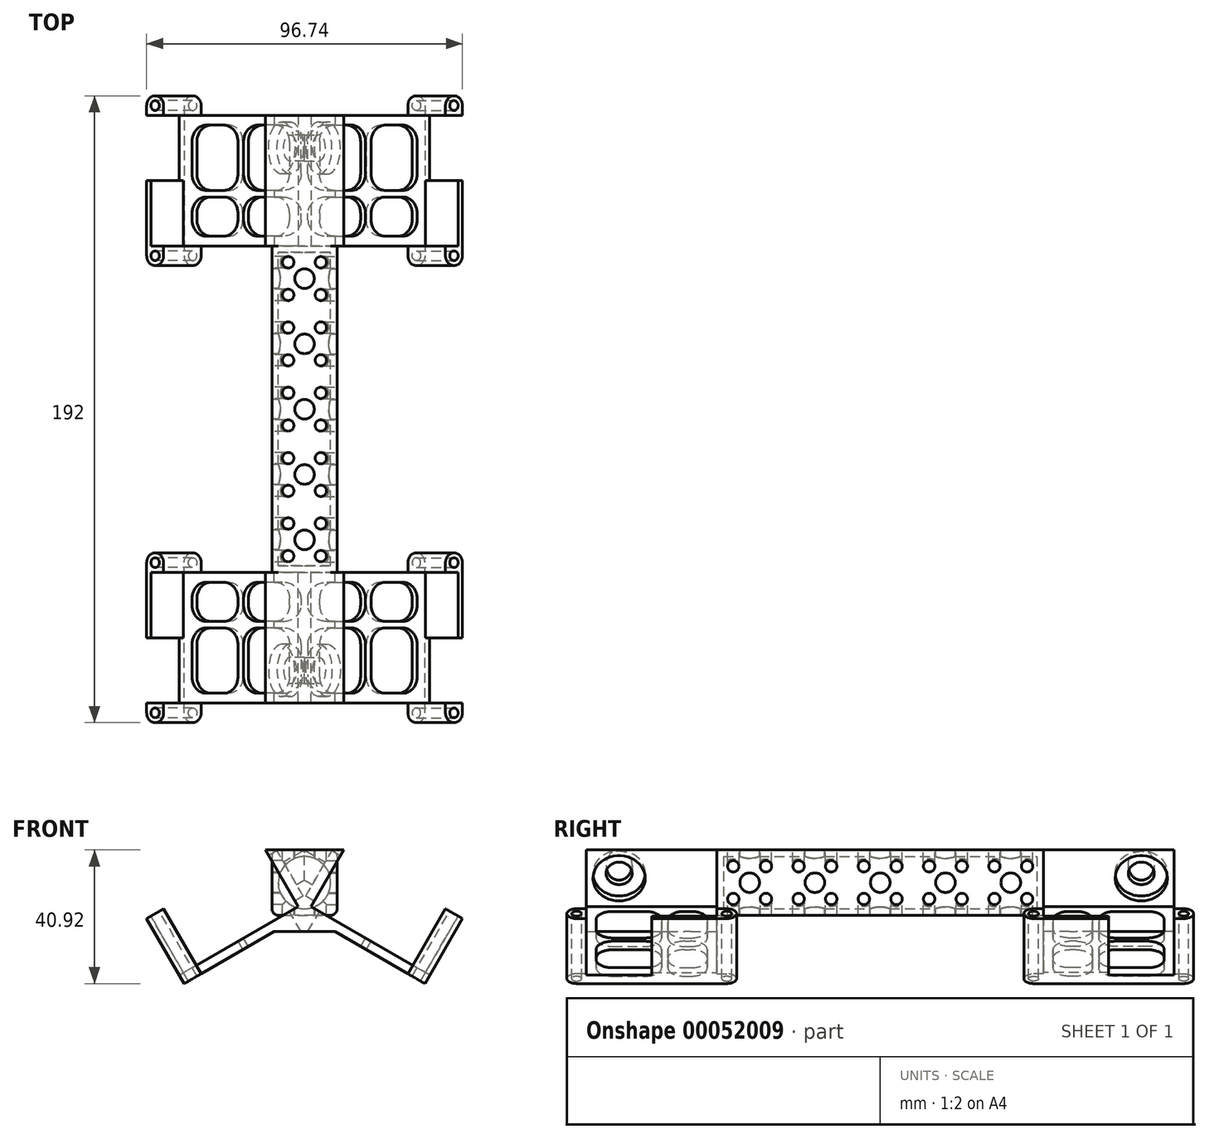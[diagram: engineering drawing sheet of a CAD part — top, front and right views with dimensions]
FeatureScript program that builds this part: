
annotation { "Feature Type Name" : "Feature", "Feature Type Description" : "" }
export const myFeature = defineFeature(function(context is Context, id is Id, definition is map)
    precondition{}
    {
        {
            var Q0;
            Q0=qCreatedBy(makeId("Front.planeOp"),FACE);
            var sketch = newSketch(context, id + "F0", { "sketchPlane" : qUnion([Q0])});
            skLineSegment(sketch, "E0.bottom", {"start": v(0, 10) * mm, "end": v(10, 10) * mm});
            skLineSegment(sketch, "E0.top", {"start": v(0, -10) * mm, "end": v(10, -10) * mm});
            skLineSegment(sketch, "E0.left", {"start": v(0, 10) * mm, "end": v(0, -10) * mm});
            skLineSegment(sketch, "E0.right", {"start": v(10, 10) * mm, "end": v(10, -10) * mm});
            skPoint(sketch, "E1", {"position": v(0, 0) * mm});
            skSolve(sketch);
        }
        {
            var Q0;
            Q0=makeQuery(id+"F0.imprint","IMPRINT",FACE,{"disambiguationData":[TD([[makeQuery(id+"F0.imprint","IMPRINT",EDGE,{"derivedFrom":sQuery(id+"F0.wireOp",EDGE,"E0.bottom")}),-1.0]])]});
            extrude(context, id + "F1", {"entities" : qUnion([Q0]), "depth" : 50 * mm, "offsetDistance" : 25 * mm});
        }
        {
            var Q0;
            Q0=makeQuery(id+"F1.opExtrude","CAP_FACE",FACE,{"disambiguationData":[OSD([sQuery(id+"F0.wireOp",EDGE,"E0.bottom"),sQuery(id+"F0.wireOp",EDGE,"E0.top"),sQuery(id+"F0.wireOp",EDGE,"E0.left"),sQuery(id+"F0.wireOp",EDGE,"E0.right")])],"isStart":false});
            var sketch = newSketch(context, id + "F2", { "sketchPlane" : qUnion([Q0])});
            skLineSegment(sketch, "E2", {"start": v(12, 10) * mm, "end": v(0.5, -9.92) * mm});
            skLineSegment(sketch, "E3", {"start": v(0.5, -9.92) * mm, "end": v(36.87, -30.92) * mm});
            skLineSegment(sketch, "E4", {"start": v(36.87, -30.92) * mm, "end": v(48.37, -11) * mm});
            skLineSegment(sketch, "E5", {"start": v(48.37, -11) * mm, "end": v(12, 10) * mm});
            skLineSegment(sketch, "E6", {"start": v(12, 10) * mm, "end": v(10, 10) * mm});
            skLineSegment(sketch, "E7", {"start": v(9.3, -15) * mm, "end": v(0, -15) * mm});
            skLineSegment(sketch, "E8", {"start": v(0, -15) * mm, "end": v(0, -10) * mm});
            skSolve(sketch);
        }
        {
            var Q0;
            {var subQ4=makeQuery(id+"F1.opExtrude","CAP_EDGE",EDGE,{"disambiguationData":[OSD([sQuery(id+"F0.wireOp",EDGE,"E0.bottom")])],"isStart":false});Q0=makeQuery(id+"F2.imprint","IMPRINT",FACE,{"disambiguationData":[TD([[makeQuery(id+"F2.imprint","IMPRINT",EDGE,{"derivedFrom":subQ4}),-1.0]])]});}
            var Q1;
            Q1=makeQuery(id+"F2.imprint","IMPRINT",FACE,{"disambiguationData":[TD([[makeQuery(id+"F2.imprint","IMPRINT",EDGE,{"derivedFrom":sQuery(id+"F2.wireOp",EDGE,"E3")}),1.0]])]});
            var Q2;
            {var subQ1=makeQuery(id+"F1.opExtrude","CAP_EDGE",EDGE,{"disambiguationData":[OSD([sQuery(id+"F0.wireOp",EDGE,"E0.top")])],"isStart":false});Q2=makeQuery(id+"F2.imprint","IMPRINT",FACE,{"disambiguationData":[TD([[makeQuery(id+"F2.imprint","IMPRINT",EDGE,{"derivedFrom":subQ1}),1.0]])]});}
            var Q3;
            {var subQ0=sQuery(id+"F2.wireOp",EDGE,"E6");Q3=makeQuery(id+"F2.imprint","IMPRINT",FACE,{"disambiguationData":[TD([[makeQuery(id+"F2.imprint","IMPRINT",EDGE,{"derivedFrom":subQ0}),1.0]])]});}
            var Q4;
            {var subQ0=sQuery(id+"F2.wireOp",EDGE,"E4");Q4=makeQuery(id+"F2.imprint","IMPRINT",FACE,{"disambiguationData":[TD([[makeQuery(id+"F2.imprint","IMPRINT",EDGE,{"derivedFrom":subQ0}),1.0]])]});}
            var Q5;
            {var subQ0=sQuery(id+"F2.wireOp",EDGE,"E7");Q5=makeQuery(id+"F2.imprint","IMPRINT",FACE,{"disambiguationData":[TD([[makeQuery(id+"F2.imprint","IMPRINT",EDGE,{"derivedFrom":subQ0}),-1.0]])]});}
            extrude(context, id + "F3", {"entities" : qUnion([Q0, Q1, Q2, Q3, Q4, Q5]), "operationType" : NewBodyOperationType.ADD, "depth" : 40 * mm, "offsetDistance" : 25 * mm});
        }
        {
            var Q0;
            Q0=makeQuery(id+"F3.opExtrude","SWEPT_FACE",FACE,{"disambiguationData":[OSD([sQuery(id+"F2.wireOp",EDGE,"E5")])]});
            var sketch = newSketch(context, id + "F4", { "sketchPlane" : qUnion([Q0])});
            skLineSegment(sketch, "E9.bottom", {"start": v(5.4, -90) * mm, "end": v(45.9, -90) * mm});
            skLineSegment(sketch, "E9.top", {"start": v(5.4, -50) * mm, "end": v(45.9, -50) * mm});
            skLineSegment(sketch, "E9.left", {"start": v(5.4, -90) * mm, "end": v(5.4, -50) * mm});
            skLineSegment(sketch, "E9.right", {"start": v(45.9, -90) * mm, "end": v(45.9, -50) * mm});
            skPoint(sketch, "E10", {"position": v(5.4, -70) * mm});
            skLineSegment(sketch, "E11.bottom", {"start": v(47.4, -90) * mm, "end": v(45.9, -90) * mm});
            skLineSegment(sketch, "E11.top", {"start": v(47.4, -70) * mm, "end": v(45.9, -70) * mm});
            skLineSegment(sketch, "E11.left", {"start": v(47.4, -90) * mm, "end": v(47.4, -70) * mm});
            skLineSegment(sketch, "E11.right", {"start": v(45.9, -90) * mm, "end": v(45.9, -70) * mm});
            skCircle(sketch, "E12", {"center": v(44.4, -93) * mm, "radius": 1.5 * mm});
            skCircle(sketch, "E13", {"center": v(44.4, -93) * mm, "radius": 3 * mm});
            skCircle(sketch, "E14", {"center": v(44.4, -47) * mm, "radius": 1.5 * mm});
            skCircle(sketch, "E15", {"center": v(44.4, -47) * mm, "radius": 3 * mm});
            skLineSegment(sketch, "E16", {"start": v(47.4, -90) * mm, "end": v(47.4, -93) * mm});
            skLineSegment(sketch, "E17", {"start": v(47.4, -50) * mm, "end": v(47.4, -47) * mm});
            skLineSegment(sketch, "E18", {"start": v(41.4, -93) * mm, "end": v(41.4, -90) * mm});
            skLineSegment(sketch, "E19", {"start": v(41.4, -47) * mm, "end": v(41.4, -50) * mm});
            skSolve(sketch);
        }
        {
            var Q0;
            Q0=makeQuery(id+"F4.imprint","IMPRINT",FACE,{"disambiguationData":[TD([[makeQuery(id+"F4.imprint","IMPRINT",EDGE,{"derivedFrom":sQuery(id+"F4.wireOp",EDGE,"E12")}),-1.0]])]});
            var Q1;
            Q1=makeQuery(id+"F4.imprint","IMPRINT",FACE,{"disambiguationData":[TD([[makeQuery(id+"F4.imprint","IMPRINT",EDGE,{"derivedFrom":sQuery(id+"F4.wireOp",EDGE,"E14")}),-1.0]])]});
            var Q2;
            {var subQ0=sQuery(id+"F4.wireOp",EDGE,"E19");Q2=makeQuery(id+"F4.imprint","IMPRINT",FACE,{"disambiguationData":[TD([[makeQuery(id+"F4.imprint","IMPRINT",EDGE,{"derivedFrom":subQ0}),1.0]])]});}
            var Q3;
            {var subQ6=sQuery(id+"F4.wireOp",EDGE,"E17");Q3=makeQuery(id+"F4.imprint","IMPRINT",FACE,{"disambiguationData":[TD([[makeQuery(id+"F4.imprint","IMPRINT",EDGE,{"derivedFrom":subQ6}),1.0]])]});}
            var Q4;
            {var subQ0=sQuery(id+"F4.wireOp",EDGE,"E18");Q4=makeQuery(id+"F4.imprint","IMPRINT",FACE,{"disambiguationData":[TD([[makeQuery(id+"F4.imprint","IMPRINT",EDGE,{"derivedFrom":subQ0}),-1.0]])]});}
            var Q5;
            {var subQ0=sQuery(id+"F4.wireOp",EDGE,"E11.bottom");Q5=makeQuery(id+"F4.imprint","IMPRINT",FACE,{"disambiguationData":[TD([[makeQuery(id+"F4.imprint","IMPRINT",EDGE,{"derivedFrom":subQ0}),1.0]])]});}
            var Q6;
            Q6=makeQuery(id+"F3.opExtrude","SWEPT_FACE",FACE,{"disambiguationData":[OSD([sQuery(id+"F2.wireOp",EDGE,"E3")])]});
            extrude(context, id + "F5", {"entities" : qUnion([Q0, Q1, Q2, Q3, Q4, Q5]), "operationType" : NewBodyOperationType.ADD, "endBound" : BoundingType.UP_TO_SURFACE, "oppositeDirection" : true, "depth" : 25 * mm, "endBoundEntityFace" : qUnion([Q6]), "offsetDistance" : 25 * mm});
        }
        {
            var Q0;
            {var subQ0=sQuery(id+"F2.wireOp",EDGE,"E5");Q0=makeQuery(id+"F5.boolean.opBoolean","MERGE",FACE,{"derivedFrom":[makeQuery(id+"F3.opExtrude","SWEPT_FACE",FACE,{"disambiguationData":[OSD([subQ0])]}),makeQuery(id+"F5.opExtrude","CAP_FACE",FACE,{"disambiguationData":[OSD([sQuery(id+"F4.wireOp",EDGE,"E9.bottom"),sQuery(id+"F4.wireOp",EDGE,"E11.bottom"),sQuery(id+"F4.wireOp",EDGE,"E12"),sQuery(id+"F4.wireOp",EDGE,"E13"),sQuery(id+"F4.wireOp",EDGE,"E16"),sQuery(id+"F4.wireOp",EDGE,"E18")])],"isStart":true}),makeQuery(id+"F5.opExtrude","CAP_FACE",FACE,{"disambiguationData":[OSD([subQ0,sQuery(id+"F4.wireOp",EDGE,"E9.top"),sQuery(id+"F4.wireOp",EDGE,"E14"),sQuery(id+"F4.wireOp",EDGE,"E15"),sQuery(id+"F4.wireOp",EDGE,"E17"),sQuery(id+"F4.wireOp",EDGE,"E19")])],"isStart":true})]});}
            var sketch = newSketch(context, id + "F6", { "sketchPlane" : qUnion([Q0])});
            skLineSegment(sketch, "E20.bottom", {"start": v(5.4, -90) * mm, "end": v(45.9, -90) * mm});
            skLineSegment(sketch, "E20.top", {"start": v(5.4, -50) * mm, "end": v(45.9, -50) * mm});
            skLineSegment(sketch, "E20.left", {"start": v(5.4, -90) * mm, "end": v(5.4, -50) * mm});
            skLineSegment(sketch, "E20.right", {"start": v(45.9, -90) * mm, "end": v(45.9, -50) * mm});
            skPoint(sketch, "E21", {"position": v(5.4, -70) * mm});
            skLineSegment(sketch, "E22.bottom", {"start": v(47.4, -90) * mm, "end": v(45.9, -90) * mm});
            skLineSegment(sketch, "E22.top", {"start": v(47.4, -70) * mm, "end": v(45.9, -70) * mm});
            skLineSegment(sketch, "E22.left", {"start": v(47.4, -90) * mm, "end": v(47.4, -70) * mm});
            skLineSegment(sketch, "E22.right", {"start": v(45.9, -90) * mm, "end": v(45.9, -70) * mm});
            skCircle(sketch, "E23", {"center": v(44.4, -93) * mm, "radius": 1.5 * mm});
            skCircle(sketch, "E24", {"center": v(44.4, -93) * mm, "radius": 3 * mm});
            skCircle(sketch, "E25", {"center": v(44.4, -47) * mm, "radius": 1.5 * mm});
            skCircle(sketch, "E26", {"center": v(44.4, -47) * mm, "radius": 3 * mm});
            skLineSegment(sketch, "E27", {"start": v(47.4, -90) * mm, "end": v(47.4, -93) * mm});
            skLineSegment(sketch, "E28", {"start": v(47.4, -60) * mm, "end": v(47.4, -47) * mm});
            skLineSegment(sketch, "E29", {"start": v(41.4, -93) * mm, "end": v(41.4, -90) * mm});
            skLineSegment(sketch, "E30", {"start": v(41.4, -47) * mm, "end": v(41.4, -50) * mm});
            skSolve(sketch);
        }
        {
            var Q0;
            Q0=makeQuery(id+"F6.imprint","IMPRINT",FACE,{"disambiguationData":[TD([[makeQuery(id+"F6.imprint","IMPRINT",EDGE,{"derivedFrom":sQuery(id+"F6.wireOp",EDGE,"E22.bottom")}),-1.0]])]});
            var Q1;
            {var subQ0=sQuery(id+"F6.wireOp",EDGE,"E20.left");Q1=makeQuery(id+"F6.imprint","IMPRINT",FACE,{"disambiguationData":[TD([[makeQuery(id+"F6.imprint","IMPRINT",EDGE,{"derivedFrom":subQ0}),-1.0]])]});}
            extrude(context, id + "F7", {"entities" : qUnion([Q0, Q1]), "operationType" : NewBodyOperationType.REMOVE, "oppositeDirection" : true, "depth" : 20 * mm, "offsetDistance" : 25 * mm});
        }
        {
            var Q0;
            Q0=makeQuery(id+"F7.boolean.opBoolean","COPY",FACE,{"derivedFrom":makeQuery(id+"F7.opExtrude","SWEPT_FACE",FACE,{"disambiguationData":[OSD([sQuery(id+"F6.wireOp",EDGE,"E20.left")])]})});
            var sketch = newSketch(context, id + "F8", { "sketchPlane" : qUnion([Q0])});
            skLineSegment(sketch, "E31.bottom", {"start": v(-90, 14.66) * mm, "end": v(-70, 14.66) * mm});
            skLineSegment(sketch, "E31.top", {"start": v(-90, -5.34) * mm, "end": v(-70, -5.34) * mm});
            skLineSegment(sketch, "E31.left", {"start": v(-90, 14.66) * mm, "end": v(-90, -5.34) * mm});
            skLineSegment(sketch, "E31.right", {"start": v(-70, 14.66) * mm, "end": v(-70, -5.34) * mm});
            skLineSegment(sketch, "E32", {"start": v(-90, 14.66) * mm, "end": v(-70, -5.34) * mm});
            skPoint(sketch, "E33", {"position": v(-80, 4.66) * mm});
            skSolve(sketch);
        }
        {
            var Q0;
            Q0=sQuery(id+"F8.wireOp",VERTEX,"E33");
            var Q1;
            Q1=makeQuery(id+"F1.opExtrude","SWEPT_BODY",BODY,{"disambiguationData":[OSD([sQuery(id+"F0.wireOp",EDGE,"E0.bottom"),sQuery(id+"F0.wireOp",EDGE,"E0.top"),sQuery(id+"F0.wireOp",EDGE,"E0.left"),sQuery(id+"F0.wireOp",EDGE,"E0.right")])]});
            hole(context, id + "F9", {"style" : HoleStyle.C_BORE, "endStyle" : HoleEndStyle.BLIND, "holeDiameter" : 8 * mm, "cBoreDiameter" : 16 * mm, "cBoreDepth" : 3 * mm, "majorDiameter" : 5 * mm, "holeDepth" : 10 * mm, "isTappedThrough" : true, "tappedDepth" : 12 * mm, "tapClearance" : 3, "locations" : qUnion([Q0]), "scope" : qUnion([Q1])});
        }
        {
            var Q0;
            Q0=makeQuery(id+"F1.opExtrude","CAP_FACE",FACE,{"disambiguationData":[OSD([sQuery(id+"F0.wireOp",EDGE,"E0.bottom"),sQuery(id+"F0.wireOp",EDGE,"E0.top"),sQuery(id+"F0.wireOp",EDGE,"E0.left"),sQuery(id+"F0.wireOp",EDGE,"E0.right")])],"isStart":true});
            var sketch = newSketch(context, id + "F10", { "sketchPlane" : qUnion([Q0])});
            skPoint(sketch, "E34", {"position": v(0, 0) * mm});
            skCircle(sketch, "E35", {"center": v(0, 0) * mm, "radius": 8 * mm});
            skSolve(sketch);
        }
        {
            var Q0;
            {var subQ0=sQuery(id+"F10.wireOp",EDGE,"E35");var subQ1=makeQuery(id+"F1.opExtrude","CAP_EDGE",EDGE,{"disambiguationData":[OSD([sQuery(id+"F0.wireOp",EDGE,"E0.left")])],"isStart":true});var subQ2=makeQuery(id+"F10.imprint","INTERSECT",VERTEX,{"disambiguationData":[OD(0.0)],"derivedFrom":[subQ1,subQ0]});Q0=makeQuery(id+"F10.imprint","IMPRINT",FACE,{"disambiguationData":[TD([[makeQuery(id+"F10.imprint","IMPRINT",EDGE,{"disambiguationData":[TD([[subQ2,-1.0]])],"derivedFrom":subQ0}),1.0]])]});}
            extrude(context, id + "F11", {"entities" : qUnion([Q0]), "operationType" : NewBodyOperationType.REMOVE, "oppositeDirection" : true, "depth" : 48 * mm, "offsetDistance" : 25 * mm});
        }
        {
            var Q0;
            Q0=makeQuery(id+"F7.boolean.opBoolean","COPY",FACE,{"derivedFrom":makeQuery(id+"F7.opExtrude","CAP_FACE",FACE,{"disambiguationData":[OSD([sQuery(id+"F6.wireOp",EDGE,"E20.bottom"),sQuery(id+"F6.wireOp",EDGE,"E20.top"),sQuery(id+"F6.wireOp",EDGE,"E20.left"),sQuery(id+"F6.wireOp",EDGE,"E20.right"),sQuery(id+"F6.wireOp",EDGE,"E22.bottom"),sQuery(id+"F6.wireOp",EDGE,"E22.top"),sQuery(id+"F6.wireOp",EDGE,"E22.left")])],"isStart":false})});
            var sketch = newSketch(context, id + "F12", { "sketchPlane" : qUnion([Q0])});
            skLineSegment(sketch, "E36.bottom", {"start": v(26.64, -65) * mm, "end": v(42.9, -65) * mm});
            skLineSegment(sketch, "E36.top", {"start": v(26.64, -53) * mm, "end": v(42.9, -53) * mm});
            skLineSegment(sketch, "E36.left", {"start": v(26.64, -65) * mm, "end": v(26.64, -53) * mm});
            skLineSegment(sketch, "E36.right", {"start": v(42.9, -65) * mm, "end": v(42.9, -53) * mm});
            skLineSegment(sketch, "E37.bottom", {"start": v(8.4, -65) * mm, "end": v(24.64, -65) * mm});
            skLineSegment(sketch, "E37.top", {"start": v(8.4, -53) * mm, "end": v(24.64, -53) * mm});
            skLineSegment(sketch, "E37.left", {"start": v(8.4, -65) * mm, "end": v(8.4, -53) * mm});
            skLineSegment(sketch, "E37.right", {"start": v(24.64, -65) * mm, "end": v(24.64, -53) * mm});
            skLineSegment(sketch, "E38.bottom", {"start": v(8.4, -87) * mm, "end": v(24.64, -87) * mm});
            skLineSegment(sketch, "E38.top", {"start": v(8.4, -67) * mm, "end": v(24.64, -67) * mm});
            skLineSegment(sketch, "E38.left", {"start": v(8.4, -87) * mm, "end": v(8.4, -67) * mm});
            skLineSegment(sketch, "E38.right", {"start": v(24.64, -87) * mm, "end": v(24.64, -67) * mm});
            skLineSegment(sketch, "E39.bottom", {"start": v(26.64, -87) * mm, "end": v(42.9, -87) * mm});
            skLineSegment(sketch, "E39.top", {"start": v(26.64, -67) * mm, "end": v(42.9, -67) * mm});
            skLineSegment(sketch, "E39.left", {"start": v(26.64, -87) * mm, "end": v(26.64, -67) * mm});
            skLineSegment(sketch, "E39.right", {"start": v(42.9, -87) * mm, "end": v(42.9, -67) * mm});
            skSolve(sketch);
        }
        {
            var Q0;
            Q0=makeQuery(id+"F12.imprint","IMPRINT",FACE,{"disambiguationData":[TD([[makeQuery(id+"F12.imprint","IMPRINT",EDGE,{"derivedFrom":sQuery(id+"F12.wireOp",EDGE,"E38.bottom")}),1.0]])]});
            var Q1;
            Q1=makeQuery(id+"F12.imprint","IMPRINT",FACE,{"disambiguationData":[TD([[makeQuery(id+"F12.imprint","IMPRINT",EDGE,{"derivedFrom":sQuery(id+"F12.wireOp",EDGE,"E37.bottom")}),1.0]])]});
            var Q2;
            Q2=makeQuery(id+"F12.imprint","IMPRINT",FACE,{"disambiguationData":[TD([[makeQuery(id+"F12.imprint","IMPRINT",EDGE,{"derivedFrom":sQuery(id+"F12.wireOp",EDGE,"E36.bottom")}),1.0]])]});
            var Q3;
            Q3=makeQuery(id+"F12.imprint","IMPRINT",FACE,{"disambiguationData":[TD([[makeQuery(id+"F12.imprint","IMPRINT",EDGE,{"derivedFrom":sQuery(id+"F12.wireOp",EDGE,"E39.bottom")}),1.0]])]});
            extrude(context, id + "F13", {"entities" : qUnion([Q0, Q1, Q2, Q3]), "operationType" : NewBodyOperationType.REMOVE, "endBound" : BoundingType.THROUGH_ALL, "oppositeDirection" : true, "depth" : 3 * mm, "offsetDistance" : 25 * mm});
        }
        {
            var Q0;
            Q0=makeQuery(id+"F1.opExtrude","SWEPT_FACE",FACE,{"disambiguationData":[OSD([sQuery(id+"F0.wireOp",EDGE,"E0.right")])]});
            var sketch = newSketch(context, id + "F14", { "sketchPlane" : qUnion([Q0])});
            skLineSegment(sketch, "E40", {"start": v(0, 0) * mm, "end": v(-20, 0) * mm});
            skLineSegment(sketch, "E41", {"start": v(-20, 0) * mm, "end": v(-40, 0) * mm});
            skSolve(sketch);
        }
        {
            var Q0;
            Q0=sQuery(id+"F14.wireOp",VERTEX,"E40.start");
            var Q1;
            Q1=sQuery(id+"F14.wireOp",VERTEX,"E41.start");
            var Q2;
            Q2=sQuery(id+"F14.wireOp",VERTEX,"E41.end");
            var Q3;
            Q3=makeQuery(id+"F1.opExtrude","SWEPT_BODY",BODY,{"disambiguationData":[OSD([sQuery(id+"F0.wireOp",EDGE,"E0.bottom"),sQuery(id+"F0.wireOp",EDGE,"E0.top"),sQuery(id+"F0.wireOp",EDGE,"E0.left"),sQuery(id+"F0.wireOp",EDGE,"E0.right")])]});
            hole(context, id + "F15", {"style" : HoleStyle.SIMPLE, "endStyle" : HoleEndStyle.THROUGH, "holeDiameter" : 6 * mm, "majorDiameter" : 5 * mm, "isTappedThrough" : true, "tappedDepth" : 12 * mm, "tapClearance" : 3, "locations" : qUnion([Q0, Q1, Q2]), "scope" : qUnion([Q3])});
        }
        {
            var Q0;
            {var subQ0=sQuery(id+"F0.wireOp",EDGE,"E0.bottom");Q0=makeQuery(id+"F3.boolean.opBoolean","MERGE",FACE,{"derivedFrom":[makeQuery(id+"F1.opExtrude","SWEPT_FACE",FACE,{"disambiguationData":[OSD([subQ0])]}),makeQuery(id+"F3.opExtrude","SWEPT_FACE",FACE,{"disambiguationData":[OSD([subQ0,sQuery(id+"F2.wireOp",EDGE,"E6")])]})]});}
            var sketch = newSketch(context, id + "F16", { "sketchPlane" : qUnion([Q0])});
            skLineSegment(sketch, "E42", {"start": v(0, 0) * mm, "end": v(0, -20) * mm});
            skLineSegment(sketch, "E43", {"start": v(0, -20) * mm, "end": v(0, -40) * mm});
            skSolve(sketch);
        }
        {
            var Q0;
            Q0=sQuery(id+"F16.wireOp",VERTEX,"E42.start");
            var Q1;
            Q1=sQuery(id+"F16.wireOp",VERTEX,"E43.start");
            var Q2;
            Q2=sQuery(id+"F16.wireOp",VERTEX,"E43.end");
            var Q3;
            Q3=makeQuery(id+"F1.opExtrude","SWEPT_BODY",BODY,{"disambiguationData":[OSD([sQuery(id+"F0.wireOp",EDGE,"E0.bottom"),sQuery(id+"F0.wireOp",EDGE,"E0.top"),sQuery(id+"F0.wireOp",EDGE,"E0.left"),sQuery(id+"F0.wireOp",EDGE,"E0.right")])]});
            hole(context, id + "F17", {"style" : HoleStyle.SIMPLE, "endStyle" : HoleEndStyle.THROUGH, "holeDiameter" : 6 * mm, "majorDiameter" : 5 * mm, "isTappedThrough" : true, "tappedDepth" : 12 * mm, "tapClearance" : 3, "locations" : qUnion([Q0, Q1, Q2]), "scope" : qUnion([Q3])});
        }
        {
            var Q0;
            Q0=makeQuery(id+"F1.opExtrude","SWEPT_FACE",FACE,{"disambiguationData":[OSD([sQuery(id+"F0.wireOp",EDGE,"E0.right")])]});
            var sketch = newSketch(context, id + "F18", { "sketchPlane" : qUnion([Q0])});
            skLineSegment(sketch, "E44.bottom", {"start": v(-5, 5) * mm, "end": v(5, 5) * mm});
            skLineSegment(sketch, "E44.top", {"start": v(-5, -5) * mm, "end": v(5, -5) * mm});
            skLineSegment(sketch, "E44.left", {"start": v(-5, 5) * mm, "end": v(-5, -5) * mm});
            skLineSegment(sketch, "E44.right", {"start": v(5, 5) * mm, "end": v(5, -5) * mm});
            skLineSegment(sketch, "E45", {"start": v(-5, 5) * mm, "end": v(5, -5) * mm, "construction": true});
            skPoint(sketch, "E46", {"position": v(0, 0) * mm});
            skLineSegment(sketch, "E47.1.0.0", {"start": v(-25, 5) * mm, "end": v(-25, -5) * mm});
            skLineSegment(sketch, "E47.1.0.1", {"start": v(-15, 5) * mm, "end": v(-15, -5) * mm});
            skLineSegment(sketch, "E47.2.0.0", {"start": v(-45, 5) * mm, "end": v(-45, -5) * mm});
            skLineSegment(sketch, "E47.2.0.1", {"start": v(-35, 5) * mm, "end": v(-35, -5) * mm});
            skLineSegment(sketch, "E47.direction1", {"start": v(-5, -5) * mm, "end": v(-25, -5) * mm, "construction": true});
            skSolve(sketch);
        }
        {
            var Q0;
            Q0=sQuery(id+"F18.wireOp",VERTEX,"E45.start");
            var Q1;
            Q1=sQuery(id+"F18.wireOp",VERTEX,"E44.top.start");
            var Q2;
            Q2=sQuery(id+"F18.wireOp",VERTEX,"E47.1.0.1.end");
            var Q3;
            Q3=sQuery(id+"F18.wireOp",VERTEX,"E47.1.0.1.start");
            var Q4;
            Q4=sQuery(id+"F18.wireOp",VERTEX,"E47.1.0.0.start");
            var Q5;
            Q5=sQuery(id+"F18.wireOp",VERTEX,"E47.direction1.end");
            var Q6;
            Q6=sQuery(id+"F18.wireOp",VERTEX,"E47.2.0.1.end");
            var Q7;
            Q7=sQuery(id+"F18.wireOp",VERTEX,"E47.2.0.1.start");
            var Q8;
            Q8=sQuery(id+"F18.wireOp",VERTEX,"E47.2.0.0.start");
            var Q9;
            Q9=sQuery(id+"F18.wireOp",VERTEX,"E47.2.0.0.end");
            var Q10;
            Q10=makeQuery(id+"F1.opExtrude","SWEPT_BODY",BODY,{"disambiguationData":[OSD([sQuery(id+"F0.wireOp",EDGE,"E0.bottom"),sQuery(id+"F0.wireOp",EDGE,"E0.top"),sQuery(id+"F0.wireOp",EDGE,"E0.left"),sQuery(id+"F0.wireOp",EDGE,"E0.right")])]});
            hole(context, id + "F19", {"style" : HoleStyle.SIMPLE, "endStyle" : HoleEndStyle.THROUGH, "holeDiameter" : 3.5 * mm, "majorDiameter" : 5 * mm, "isTappedThrough" : true, "tappedDepth" : 12 * mm, "tapClearance" : 3, "locations" : qUnion([Q0, Q1, Q2, Q3, Q4, Q5, Q6, Q7, Q8, Q9]), "scope" : qUnion([Q10])});
        }
        {
            var Q0;
            {var subQ0=sQuery(id+"F0.wireOp",EDGE,"E0.bottom");Q0=makeQuery(id+"F3.boolean.opBoolean","MERGE",FACE,{"derivedFrom":[makeQuery(id+"F1.opExtrude","SWEPT_FACE",FACE,{"disambiguationData":[OSD([subQ0])]}),makeQuery(id+"F3.opExtrude","SWEPT_FACE",FACE,{"disambiguationData":[OSD([subQ0,sQuery(id+"F2.wireOp",EDGE,"E6")])]})]});}
            var sketch = newSketch(context, id + "F20", { "sketchPlane" : qUnion([Q0])});
            skLineSegment(sketch, "E48.bottom", {"start": v(-5, 5) * mm, "end": v(5, 5) * mm});
            skLineSegment(sketch, "E48.top", {"start": v(-5, -5) * mm, "end": v(5, -5) * mm});
            skLineSegment(sketch, "E48.left", {"start": v(-5, 5) * mm, "end": v(-5, -5) * mm});
            skLineSegment(sketch, "E48.right", {"start": v(5, 5) * mm, "end": v(5, -5) * mm});
            skLineSegment(sketch, "E49", {"start": v(-5, 5) * mm, "end": v(5, -5) * mm, "construction": true});
            skPoint(sketch, "E50", {"position": v(0, 0) * mm});
            skLineSegment(sketch, "E51.0.1.0", {"start": v(-5, -15) * mm, "end": v(5, -15) * mm});
            skLineSegment(sketch, "E51.0.1.1", {"start": v(-5, -25) * mm, "end": v(5, -25) * mm});
            skLineSegment(sketch, "E51.0.2.0", {"start": v(-5, -35) * mm, "end": v(5, -35) * mm});
            skLineSegment(sketch, "E51.0.2.1", {"start": v(-5, -45) * mm, "end": v(5, -45) * mm});
            skLineSegment(sketch, "E51.direction1", {"start": v(-5, 5) * mm, "end": v(-25, 5) * mm, "construction": true});
            skLineSegment(sketch, "E51.direction2", {"start": v(-5, 5) * mm, "end": v(-5, -15) * mm, "construction": true});
            skSolve(sketch);
        }
        {
            var Q0;
            Q0=sQuery(id+"F20.wireOp",VERTEX,"E49.end");
            var Q1;
            Q1=sQuery(id+"F20.wireOp",VERTEX,"E51.0.1.0.end");
            var Q2;
            Q2=sQuery(id+"F20.wireOp",VERTEX,"E51.0.1.1.end");
            var Q3;
            Q3=sQuery(id+"F20.wireOp",VERTEX,"E51.0.2.0.end");
            var Q4;
            Q4=sQuery(id+"F20.wireOp",VERTEX,"E51.0.2.1.end");
            var Q5;
            Q5=makeQuery(id+"F1.opExtrude","SWEPT_BODY",BODY,{"disambiguationData":[OSD([sQuery(id+"F0.wireOp",EDGE,"E0.bottom"),sQuery(id+"F0.wireOp",EDGE,"E0.top"),sQuery(id+"F0.wireOp",EDGE,"E0.left"),sQuery(id+"F0.wireOp",EDGE,"E0.right")])]});
            hole(context, id + "F21", {"style" : HoleStyle.SIMPLE, "endStyle" : HoleEndStyle.THROUGH, "holeDiameter" : 3.5 * mm, "majorDiameter" : 5 * mm, "isTappedThrough" : true, "tappedDepth" : 12 * mm, "tapClearance" : 3, "locations" : qUnion([Q0, Q1, Q2, Q3, Q4]), "scope" : qUnion([Q5])});
        }
        {
            var Q0;
            Q0=makeQuery(id+"F1.opExtrude","SWEPT_EDGE",EDGE,{"disambiguationData":[OSD([sQuery(id+"F0.wireOp",EDGE,"E0.bottom"),sQuery(id+"F0.wireOp",EDGE,"E0.right")])]});
            var Q1;
            Q1=makeQuery(id+"F1.opExtrude","SWEPT_EDGE",EDGE,{"disambiguationData":[OSD([sQuery(id+"F0.wireOp",EDGE,"E0.top"),sQuery(id+"F0.wireOp",EDGE,"E0.right")])]});
            fillet(context, id + "F22", {"entities" : qUnion([Q0, Q1]), "radius" : 2 * mm, "tangentPropagation" : true, "allowEdgeOverflow" : false});
        }
        {
            var Q0;
            Q0=makeQuery(id+"F13.boolean.opBoolean","COPY",EDGE,{"derivedFrom":makeQuery(id+"F13.opExtrude","SWEPT_EDGE",EDGE,{"disambiguationData":[OSD([sQuery(id+"F12.wireOp",EDGE,"E38.top"),sQuery(id+"F12.wireOp",EDGE,"E38.left")])]})});
            var Q1;
            Q1=makeQuery(id+"F13.boolean.opBoolean","COPY",EDGE,{"derivedFrom":makeQuery(id+"F13.opExtrude","SWEPT_EDGE",EDGE,{"disambiguationData":[OSD([sQuery(id+"F12.wireOp",EDGE,"E37.top"),sQuery(id+"F12.wireOp",EDGE,"E37.left")])]})});
            var Q2;
            Q2=makeQuery(id+"F13.boolean.opBoolean","COPY",EDGE,{"derivedFrom":makeQuery(id+"F13.opExtrude","SWEPT_EDGE",EDGE,{"disambiguationData":[OSD([sQuery(id+"F12.wireOp",EDGE,"E36.top"),sQuery(id+"F12.wireOp",EDGE,"E36.left")])]})});
            var Q3;
            Q3=makeQuery(id+"F13.boolean.opBoolean","COPY",EDGE,{"derivedFrom":makeQuery(id+"F13.opExtrude","SWEPT_EDGE",EDGE,{"disambiguationData":[OSD([sQuery(id+"F12.wireOp",EDGE,"E39.top"),sQuery(id+"F12.wireOp",EDGE,"E39.left")])]})});
            var Q4;
            Q4=makeQuery(id+"F13.boolean.opBoolean","COPY",EDGE,{"derivedFrom":makeQuery(id+"F13.opExtrude","SWEPT_EDGE",EDGE,{"disambiguationData":[OSD([sQuery(id+"F12.wireOp",EDGE,"E38.bottom"),sQuery(id+"F12.wireOp",EDGE,"E38.left")])]})});
            var Q5;
            Q5=makeQuery(id+"F13.boolean.opBoolean","COPY",EDGE,{"derivedFrom":makeQuery(id+"F13.opExtrude","SWEPT_EDGE",EDGE,{"disambiguationData":[OSD([sQuery(id+"F12.wireOp",EDGE,"E37.bottom"),sQuery(id+"F12.wireOp",EDGE,"E37.left")])]})});
            var Q6;
            Q6=makeQuery(id+"F13.boolean.opBoolean","COPY",EDGE,{"derivedFrom":makeQuery(id+"F13.opExtrude","SWEPT_EDGE",EDGE,{"disambiguationData":[OSD([sQuery(id+"F12.wireOp",EDGE,"E36.bottom"),sQuery(id+"F12.wireOp",EDGE,"E36.left")])]})});
            var Q7;
            Q7=makeQuery(id+"F13.boolean.opBoolean","COPY",EDGE,{"derivedFrom":makeQuery(id+"F13.opExtrude","SWEPT_EDGE",EDGE,{"disambiguationData":[OSD([sQuery(id+"F12.wireOp",EDGE,"E39.bottom"),sQuery(id+"F12.wireOp",EDGE,"E39.left")])]})});
            var Q8;
            Q8=makeQuery(id+"F13.boolean.opBoolean","COPY",EDGE,{"derivedFrom":makeQuery(id+"F13.opExtrude","SWEPT_EDGE",EDGE,{"disambiguationData":[OSD([sQuery(id+"F12.wireOp",EDGE,"E37.bottom"),sQuery(id+"F12.wireOp",EDGE,"E37.right")])]})});
            var Q9;
            Q9=makeQuery(id+"F13.boolean.opBoolean","COPY",EDGE,{"derivedFrom":makeQuery(id+"F13.opExtrude","SWEPT_EDGE",EDGE,{"disambiguationData":[OSD([sQuery(id+"F12.wireOp",EDGE,"E36.bottom"),sQuery(id+"F12.wireOp",EDGE,"E36.right")])]})});
            var Q10;
            Q10=makeQuery(id+"F13.boolean.opBoolean","COPY",EDGE,{"derivedFrom":makeQuery(id+"F13.opExtrude","SWEPT_EDGE",EDGE,{"disambiguationData":[OSD([sQuery(id+"F12.wireOp",EDGE,"E39.bottom"),sQuery(id+"F12.wireOp",EDGE,"E39.right")])]})});
            var Q11;
            Q11=makeQuery(id+"F13.boolean.opBoolean","COPY",EDGE,{"derivedFrom":makeQuery(id+"F13.opExtrude","SWEPT_EDGE",EDGE,{"disambiguationData":[OSD([sQuery(id+"F12.wireOp",EDGE,"E38.bottom"),sQuery(id+"F12.wireOp",EDGE,"E38.right")])]})});
            var Q12;
            Q12=makeQuery(id+"F13.boolean.opBoolean","COPY",EDGE,{"derivedFrom":makeQuery(id+"F13.opExtrude","SWEPT_EDGE",EDGE,{"disambiguationData":[OSD([sQuery(id+"F12.wireOp",EDGE,"E37.top"),sQuery(id+"F12.wireOp",EDGE,"E37.right")])]})});
            var Q13;
            Q13=makeQuery(id+"F13.boolean.opBoolean","COPY",EDGE,{"derivedFrom":makeQuery(id+"F13.opExtrude","SWEPT_EDGE",EDGE,{"disambiguationData":[OSD([sQuery(id+"F12.wireOp",EDGE,"E36.top"),sQuery(id+"F12.wireOp",EDGE,"E36.right")])]})});
            var Q14;
            Q14=makeQuery(id+"F13.boolean.opBoolean","COPY",EDGE,{"derivedFrom":makeQuery(id+"F13.opExtrude","SWEPT_EDGE",EDGE,{"disambiguationData":[OSD([sQuery(id+"F12.wireOp",EDGE,"E39.top"),sQuery(id+"F12.wireOp",EDGE,"E39.right")])]})});
            var Q15;
            Q15=makeQuery(id+"F13.boolean.opBoolean","COPY",EDGE,{"derivedFrom":makeQuery(id+"F13.opExtrude","SWEPT_EDGE",EDGE,{"disambiguationData":[OSD([sQuery(id+"F12.wireOp",EDGE,"E38.top"),sQuery(id+"F12.wireOp",EDGE,"E38.right")])]})});
            fillet(context, id + "F23", {"entities" : qUnion([Q0, Q1, Q2, Q3, Q4, Q5, Q6, Q7, Q8, Q9, Q10, Q11, Q12, Q13, Q14, Q15]), "radius" : 5 * mm, "tangentPropagation" : true, "allowEdgeOverflow" : false});
        }
        {
            var Q0;
            Q0=makeQuery(id+"F1.opExtrude","SWEPT_BODY",BODY,{"disambiguationData":[OSD([sQuery(id+"F0.wireOp",EDGE,"E0.bottom"),sQuery(id+"F0.wireOp",EDGE,"E0.top"),sQuery(id+"F0.wireOp",EDGE,"E0.left"),sQuery(id+"F0.wireOp",EDGE,"E0.right")])]});
            var Q1;
            {var subQ0=sQuery(id+"F0.wireOp",EDGE,"E0.left");Q1=makeQuery(id+"F3.boolean.opBoolean","MERGE",FACE,{"derivedFrom":[makeQuery(id+"F1.opExtrude","SWEPT_FACE",FACE,{"disambiguationData":[OSD([subQ0])]}),makeQuery(id+"F3.opExtrude","SWEPT_FACE",FACE,{"disambiguationData":[OSD([subQ0])]})]});}
            mirror(context, id + "F24", {"operationType" : NewBodyOperationType.ADD, "entities" : qUnion([Q0]), "mirrorPlane" : qUnion([Q1])});
        }
        {
            var Q0;
            Q0=makeQuery(id+"F1.opExtrude","SWEPT_BODY",BODY,{"disambiguationData":[OSD([sQuery(id+"F0.wireOp",EDGE,"E0.bottom"),sQuery(id+"F0.wireOp",EDGE,"E0.top"),sQuery(id+"F0.wireOp",EDGE,"E0.left"),sQuery(id+"F0.wireOp",EDGE,"E0.right")])]});
            var Q1;
            Q1=qCreatedBy(makeId("Front.planeOp"),FACE);
            mirror(context, id + "F25", {"operationType" : NewBodyOperationType.ADD, "entities" : qUnion([Q0]), "mirrorPlane" : qUnion([Q1])});
        }
    });
